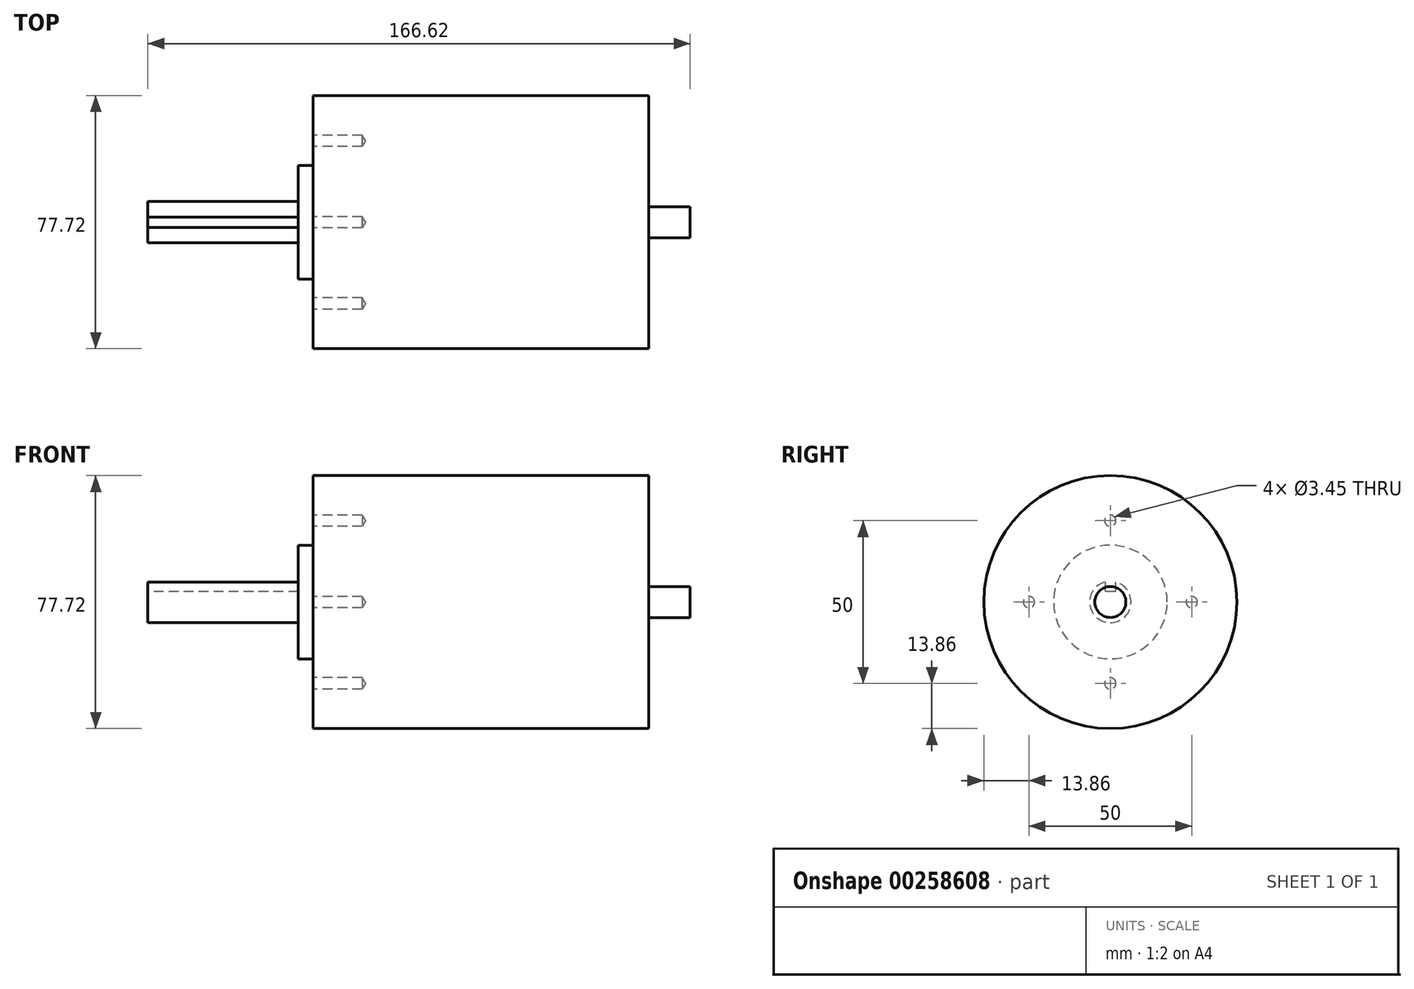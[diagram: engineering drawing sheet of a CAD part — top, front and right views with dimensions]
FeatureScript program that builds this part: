
annotation { "Feature Type Name" : "Feature", "Feature Type Description" : "" }
export const myFeature = defineFeature(function(context is Context, id is Id, definition is map)
    precondition{}
    {
        {
            var Q0;
            Q0=qCreatedBy(makeId("Front.planeOp"),FACE);
            var sketch = newSketch(context, id + "F0", { "sketchPlane" : qUnion([Q0])});
            skLineSegment(sketch, "E0", {"start": v(-73.18, 0) * mm, "end": v(226.44, 0) * mm, "construction": true});
            skLineSegment(sketch, "E1", {"start": v(0, 0) * mm, "end": v(0, 6.35) * mm});
            skLineSegment(sketch, "E2", {"start": v(0, 6.35) * mm, "end": v(46.23, 6.35) * mm});
            skLineSegment(sketch, "E3", {"start": v(50.8, 17.45) * mm, "end": v(50.8, 38.86) * mm});
            skLineSegment(sketch, "E4", {"start": v(50.8, 38.86) * mm, "end": v(153.92, 38.86) * mm});
            skLineSegment(sketch, "E5", {"start": v(153.92, 38.86) * mm, "end": v(153.92, 4.76) * mm});
            skLineSegment(sketch, "E6", {"start": v(50.8, 17.45) * mm, "end": v(46.23, 17.45) * mm});
            skLineSegment(sketch, "E7", {"start": v(46.23, 17.45) * mm, "end": v(46.23, 6.35) * mm});
            skLineSegment(sketch, "E8", {"start": v(153.92, 4.76) * mm, "end": v(166.62, 4.76) * mm});
            skLineSegment(sketch, "E9", {"start": v(166.62, 4.76) * mm, "end": v(166.62, 0) * mm});
            skLineSegment(sketch, "E10", {"start": v(0, 0) * mm, "end": v(166.62, 0) * mm});
            skSolve(sketch);
        }
        {
            var Q0;
            Q0 = qSketchRegion(id + "F0", true);
            var Q1;
            Q1=sQuery(id+"F0.wireOp",EDGE,"E0");
            revolve(context, id + "F1", {"entities" : qUnion([Q0]), "axis" : qUnion([Q1]), "revolveType" : RevolveType.FULL});
        }
        {
            var Q0;
            Q0=makeQuery(id+"F1.opRevolve","SWEPT_FACE",FACE,{"disambiguationData":[OSD([sQuery(id+"F0.wireOp",EDGE,"E1")])]});
            var sketch = newSketch(context, id + "F2", { "sketchPlane" : qUnion([Q0])});
            skLineSegment(sketch, "E11.bottom", {"start": v(-1.59, 11.63) * mm, "end": v(1.59, 11.63) * mm});
            skLineSegment(sketch, "E11.top", {"start": v(-1.59, 3.17) * mm, "end": v(1.59, 3.18) * mm});
            skLineSegment(sketch, "E11.left", {"start": v(-1.59, 11.63) * mm, "end": v(-1.59, 3.17) * mm});
            skLineSegment(sketch, "E11.right", {"start": v(1.59, 11.63) * mm, "end": v(1.59, 3.18) * mm});
            skSolve(sketch);
        }
        {
            var Q0;
            Q0 = qSketchRegion(id + "F2", true);
            var Q1;
            Q1=makeQuery(id+"F1.opRevolve","SWEPT_FACE",FACE,{"disambiguationData":[OSD([sQuery(id+"F0.wireOp",EDGE,"E7")])]});
            extrude(context, id + "F3", {"entities" : qUnion([Q0]), "operationType" : NewBodyOperationType.REMOVE, "endBound" : BoundingType.UP_TO_SURFACE, "oppositeDirection" : true, "endBoundEntityFace" : qUnion([Q1]), "depth" : 25.4 * mm});
        }
        {
            var Q0;
            Q0=makeQuery(id+"F1.opRevolve","SWEPT_FACE",FACE,{"disambiguationData":[OSD([sQuery(id+"F0.wireOp",EDGE,"E3")])]});
            var sketch = newSketch(context, id + "F4", { "sketchPlane" : qUnion([Q0])});
            skPoint(sketch, "E12", {"position": v(-25, 0) * mm});
            skPoint(sketch, "E13", {"position": v(0, 25) * mm});
            skPoint(sketch, "E14", {"position": v(0, -25) * mm});
            skPoint(sketch, "E15", {"position": v(25, 0) * mm});
            skCircle(sketch, "E16", {"center": v(0, 0) * mm, "radius": 25 * mm, "construction": true});
            skSolve(sketch);
        }
        {
            var Q0;
            Q0=sQuery(id+"F4.wireOp",VERTEX,"E12");
            var Q1;
            Q1=sQuery(id+"F4.wireOp",VERTEX,"E14");
            var Q2;
            Q2=sQuery(id+"F4.wireOp",VERTEX,"E15");
            var Q3;
            Q3=sQuery(id+"F4.wireOp",VERTEX,"E13");
            var Q4;
            Q4=makeQuery(id+"F1.opRevolve","SWEPT_BODY",BODY,{"disambiguationData":[OSD([sQuery(id+"F0.wireOp",EDGE,"E1"),sQuery(id+"F0.wireOp",EDGE,"E2"),sQuery(id+"F0.wireOp",EDGE,"E3"),sQuery(id+"F0.wireOp",EDGE,"E4"),sQuery(id+"F0.wireOp",EDGE,"E5"),sQuery(id+"F0.wireOp",EDGE,"E6"),sQuery(id+"F0.wireOp",EDGE,"E7"),sQuery(id+"F0.wireOp",EDGE,"E8"),sQuery(id+"F0.wireOp",EDGE,"E9"),sQuery(id+"F0.wireOp",EDGE,"E10")])]});
            hole(context, id + "F5", {"style" : HoleStyle.SIMPLE, "endStyle" : HoleEndStyle.BLIND, "standardTappedOrClearance" : lookupTablePath({ "standard" : "ANSI", "engagement" : "75%", "pitch" : "32 tpi", "size" : "#8", "type" : "Tapped" }), "standardBlindInLast" : lookupTablePath({ "standard" : "ANSI", "engagement" : "75%", "pitch" : "32 tpi", "size" : "#8", "type" : "Tapped" }), "holeDiameter" : 3.45 * mm, "showTappedDepth" : true, "holeDepth" : 15.08 * mm, "tappedDepth" : 12.7 * mm, "tapClearance" : 3, "startFromSketch" : true, "locations" : qUnion([Q0, Q1, Q2, Q3]), "scope" : qUnion([Q4]), "majorDiameter" : 4.17 * mm});
        }
    });
